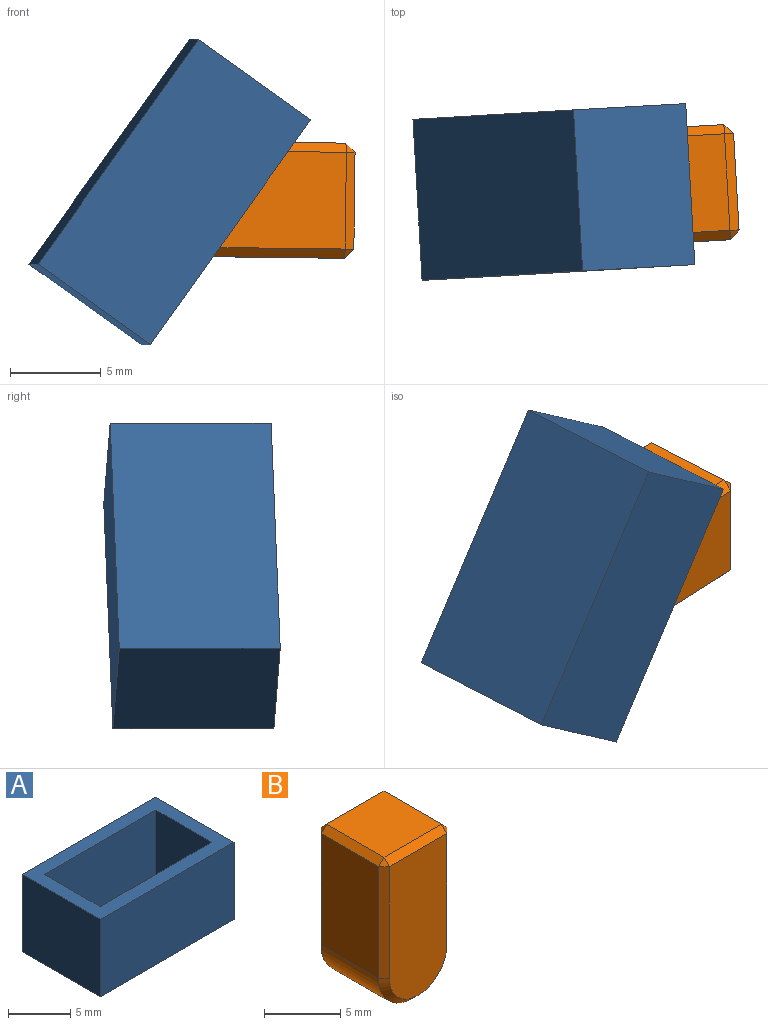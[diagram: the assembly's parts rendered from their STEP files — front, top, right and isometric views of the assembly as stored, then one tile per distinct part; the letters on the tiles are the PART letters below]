
ASSEMBLY  parts=2 mates=1
PART A: 13 faces, bbox 15.2x8.9x7.6 mm
  f0: plane 6.35x6.35mm, normal (0,1,0), area 40.3mm2, adj f1,f6,f10,f11
  f1: plane 6.35x3.18mm, normal (0,1,0), area 20.2mm2, adj f0,f7,f10,f11
  f2: plane 8.89x7.62mm, normal (-1,0,0), area 67.7mm2, adj f3,f9,f10,f12
  f3: plane 15.24x7.62mm, normal (0,-1,0), area 116.1mm2, adj f2,f4,f10,f12
  f4: plane 8.89x7.62mm, normal (1,0,0), area 67.7mm2, adj f3,f9,f10,f12
  f5: plane 6.35x6.35mm, normal (-1,0,0), area 40.3mm2, adj f6,f8,f10,f11
  f6: plane 6.35x3.18mm, normal (0,1,0), area 20.2mm2, adj f0,f5,f10,f11
  f7: plane 6.35x6.35mm, normal (1,0,0), area 40.3mm2, adj f1,f8,f10,f11
  f8: plane 12.7x6.35mm, normal (0,-1,0), area 80.6mm2, adj f5,f7,f10,f11
  f9: plane 15.24x7.62mm, normal (0,1,0), area 116.1mm2, adj f2,f4,f10,f12
  f10: plane 15.24x8.89mm, normal (0,0,1), area 54.8mm2, adj f0,f1,f2,f3,f4,f5,f6,f7
  f11: plane 12.7x6.35mm, normal (0,0,1), area 80.6mm2, adj f0,f1,f5,f6,f7,f8
  f12: plane 15.24x8.89mm, normal (0,0,-1), area 135.5mm2, adj f2,f3,f4,f9
PART B: 20 faces, bbox 6.4x6.4x12.7 mm
  f0: plane 11.68x5.33mm, normal (0,-1,0), area 59.3mm2, adj f6,f10,f13,f14
  f1: plane 9.02x5.33mm, normal (1,0,0), area 48.1mm2, adj f5,f6,f7,f8
  f2: plane 11.68x5.33mm, normal (0,1,0), area 59.3mm2, adj f7,f11,f15,f16
  f3: plane 9.02x5.33mm, normal (-1,0,0), area 48.1mm2, adj f5,f14,f15,f19
  f4: plane 5.33x5.33mm, normal (0,0,1), area 28.5mm2, adj f8,f13,f16,f19
  f5: cylinder r=3.17mm len=6.35mm, axis (0,-1,0), area 53.2mm2, adj f1,f3,f10,f11
  f6: plane 9.02x0.51mm, normal (0.71,-0.71,0), area 6.5mm2, adj f0,f1,f9,f10
  f7: plane 9.02x0.51mm, normal (0.71,0.71,0), area 6.5mm2, adj f1,f2,f11,f12
  f8: plane 5.33x0.51mm, normal (0.71,0,0.71), area 3.8mm2, adj f1,f4,f9,f12
  f9: plane 0.51x0.51mm, normal (0.58,-0.58,0.58), area 0.2mm2, adj f6,f8,f13
  f10: cone r=2.67mm half-angle=45deg, axis (0,1,0), area 6.6mm2, adj f0,f5,f6,f14
  f11: cone r=2.67mm half-angle=45deg, axis (0,-1,0), area 6.6mm2, adj f2,f5,f7,f15
  f12: plane 0.51x0.51mm, normal (0.58,0.58,0.58), area 0.2mm2, adj f7,f8,f16
  f13: plane 5.33x0.51mm, normal (0,-0.71,0.71), area 3.8mm2, adj f0,f4,f9,f17
  f14: plane 9.02x0.51mm, normal (-0.71,-0.71,0), area 6.5mm2, adj f0,f3,f10,f17
  f15: plane 9.02x0.51mm, normal (-0.71,0.71,0), area 6.5mm2, adj f2,f3,f11,f18
  f16: plane 5.33x0.51mm, normal (0,0.71,0.71), area 3.8mm2, adj f2,f4,f12,f18
  f17: plane 0.51x0.51mm, normal (-0.58,-0.58,0.58), area 0.2mm2, adj f13,f14,f19
  f18: plane 0.51x0.51mm, normal (-0.58,0.58,0.58), area 0.2mm2, adj f15,f16,f19
  f19: plane 5.33x0.51mm, normal (-0.71,0,0.71), area 3.8mm2, adj f3,f4,f17,f18
PLACE A rot(axis=(-0.03,1,0.01),125.6deg) t=(-68.86,26.82,-11.72)mm
PLACE B rot(axis=(-0.71,-0.02,-0.7),177.7deg) t=(-46.56,28.09,80.96)mm
MATE revolute B.f5 <-> A.f0  axis (0.06,-1,0) through (-43.98,25.06,17.43)mm
